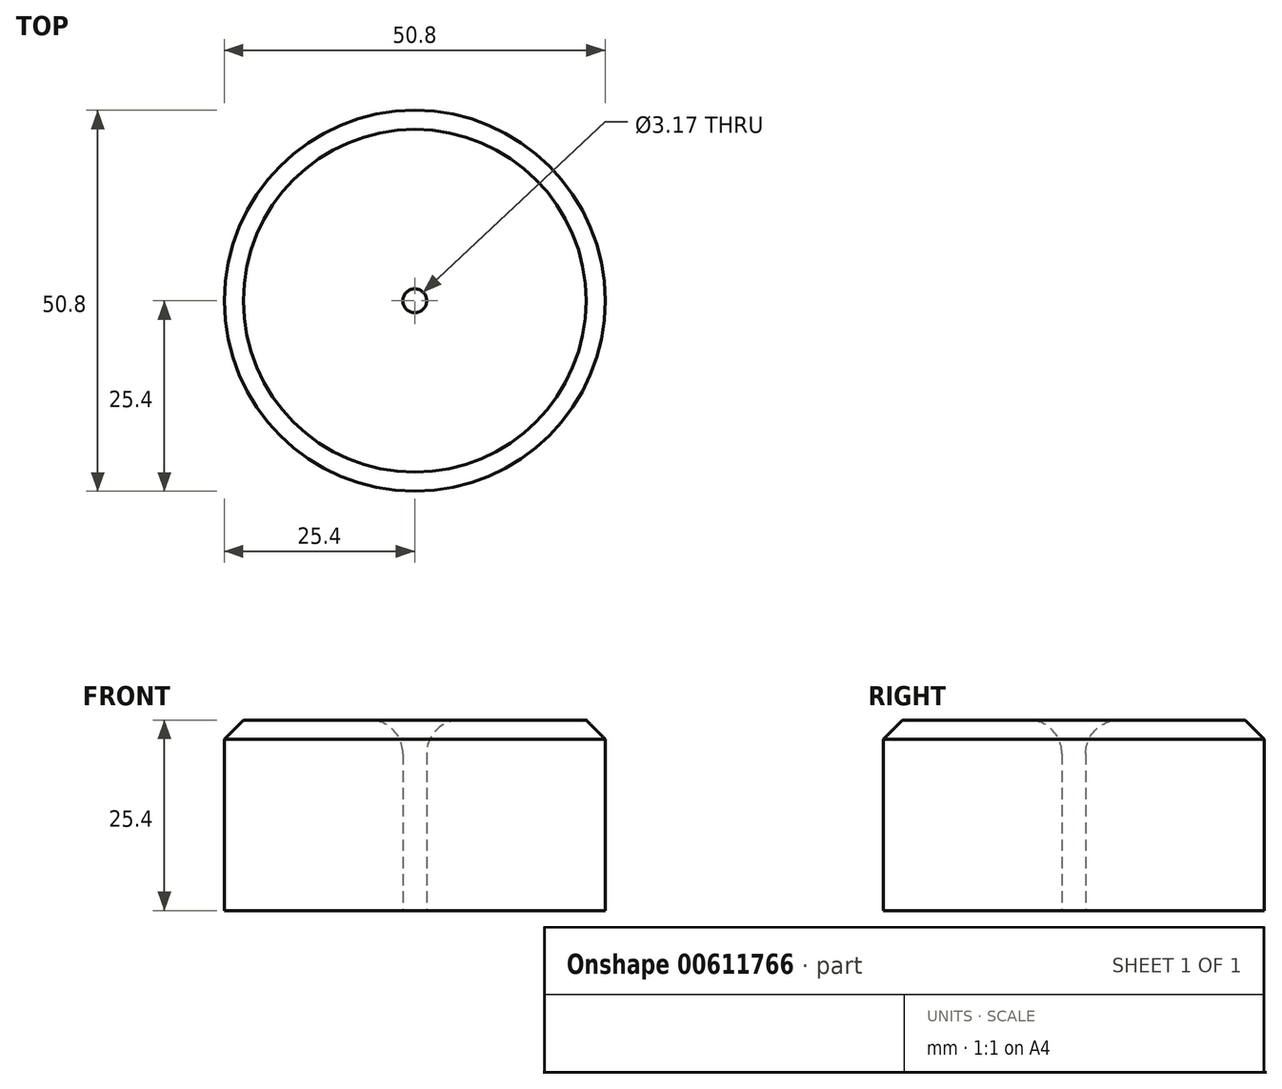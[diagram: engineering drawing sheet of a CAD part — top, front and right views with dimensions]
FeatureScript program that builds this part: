
annotation { "Feature Type Name" : "Feature", "Feature Type Description" : "" }
export const myFeature = defineFeature(function(context is Context, id is Id, definition is map)
    precondition{}
    {
        {
            var Q0;
            Q0=qCreatedBy(makeId("Top.planeOp"),FACE);
            var sketch = newSketch(context, id + "F0", { "sketchPlane" : qUnion([Q0])});
            skCircle(sketch, "E0", {"center": v(0, 0) * mm, "radius": 25.4 * mm});
            skCircle(sketch, "E1", {"center": v(0, 0) * mm, "radius": 1.59 * mm});
            skSolve(sketch);
        }
        {
            var Q0;
            Q0=makeQuery(id+"F0.imprint","IMPRINT",FACE,{"disambiguationData":[TD([[makeQuery(id+"F0.imprint","IMPRINT",EDGE,{"derivedFrom":sQuery(id+"F0.wireOp",EDGE,"E0")}),1.0]])]});
            var Q1;
            Q1=sQuery(id+"F0.wireOp",EDGE,"E0");
            extrude(context, id + "F1", {"entities" : qUnion([Q0]), "surfaceEntities" : qUnion([Q1]), "depth" : 25.4 * mm, "offsetDistance" : 25.4 * mm});
        }
        {
            var Q0;
            Q0=makeQuery(id+"F1.opExtrude","CAP_EDGE",EDGE,{"disambiguationData":[OSD([sQuery(id+"F0.wireOp",EDGE,"E0")])],"isStart":false});
            chamfer(context, id + "F2", {"entities" : qUnion([Q0]), "width" : 2.54 * mm, "tangentPropagation" : true});
        }
        {
            var Q0;
            Q0=makeQuery(id+"F1.opExtrude","CAP_EDGE",EDGE,{"disambiguationData":[OSD([sQuery(id+"F0.wireOp",EDGE,"E1")])],"isStart":false});
            fillet(context, id + "F3", {"entities" : qUnion([Q0]), "radius" : 4.44 * mm, "tangentPropagation" : true, "allowEdgeOverflow" : false});
        }
    });
